# Revit family: ICV-201G
name_source: partatom
category: Pipe Accessories
revit_build: Autodesk Revit 2017 (Build: 20160225_1515(x64)
units: mm (PartAtom-declared; Revit-internal decimal feet)

## family parameters
Always vertical = Yes
Cut with Voids When Loaded = Yes
OmniClass Number = 23.27.31.27
OmniClass Title = Globe Valves
Part Type = Valve - Normal
Round Connector Dimension = Use Diameter
Shared = No
Work Plane-Based = No

## types (6) — shared parameters
Assembly Code = G2050700
Body Material = Hunter® ABS Plastic
Current = 0 A
Filter Sentry = Factory Installed Filter Sentry ™
Flow = 150.0 L/min
Flow Max = 750.0 L/min
Flow Min = 150.0 L/min
Flow_Value = 150.0 L/min
Frequency = 60 Hz
Height = 180 mm  [stored 0.590551 ft]
Inlet Diameter = 2" (50mm)
Inner Diameter = 50 mm  [stored 0.164042 ft]
Keynote = 328423.01
Length = 170 mm  [stored 0.557743 ft]
Loss Method = K Coefficient
Manufacturer = Hunter® Industries
Outer Diameter = 63 mm  [stored 0.206693 ft]
Pipe Diameter = 63 mm  [stored 0.206693 ft]
Power = 8 VA
Power Factor = 1
Pressure Loss = 5.0 kPa
Show Valve Box = Yes
Solenoid Type = inrush
Solenoid VAC = 24 V
Tag Name = ICV-201G
Type Comments = ICV Valve
Type Image = <None>
URL = https://www.hunterindustries.com
Valid Flow = 150.0 L/min
Valve Box = Valve Box
Width = 140 mm  [stored 0.459318 ft]
zero-valued in all types: K Coefficient

## per-type parameters (varying)
| type | Accu Sync® | Accu-Sync URL | AccuSync | Description | K Coefficient Table | Max_Pressure | Min_Pressure | Model |
| ICV-201G-FS |  | ------ | without AccuSync | High Pressure Commercial System Valve ICV-201G with Filter Sentry ™ |  | 1500.0 kPa | 150.0 kPa | ICV-201G-FS |
| ICV-201G-FS-AS-ADJ Black-Adjustable Pressure | Accu Sync® AS-ADJ Black Adjustable Pressure Regulator | https://www.hunterindustries.com | AccuSync Adjustable | High Pressure Commercial System Valve ICV-201G with Filter Sentry ™ and Accu Sync® AS-ADJ Black Adjustable Pressure Regulator | Globe Valve Threaded | 700.0 kPa | 140.0 kPa | ICV-201G-FS-AS-ADJ |
| ICV-201G-FS-AS-30 Red-2.1bar | Accu Sync® Fixed AS-30 Red Fixed Pressure Regulator at 2.1 bar | https://www.hunterindustries.com | AccuSync fixed | High Pressure Commercial System Valve ICV-201G with Filter Sentry ™ and Accu Sync® AS-30 Red Fixed Pressure Regulator |  | 210.0 kPa | 210.0 kPa | ICV-201G-FS-AS-30 |
| ICV-201G-FS-AS-40 Grey-2.8bar | Accu Sync® AS-40 Grey Fixed Pressure Regulator at 2.8 bar | https://www.hunterindustries.com | AccuSync fixed | High Pressure Commercial System Valve ICV-201G with Filter Sentry ™ and Accu Sync® AS-40 Grey Fixed Pressure Regulator |  | 280.0 kPa | 280.0 kPa | ICV-201G-FS-AS-40 |
| ICV-201G-FS-AS-50 Blue-3.5bar | Accu Sync® AS-50 Blue  Fixed Pressure Regulator at 3.5 bar | https://www.hunterindustries.com | AccuSync fixed | High Pressure Commercial System Valve ICV-201G with Filter Sentry ™ and Accu Sync® AS-50 Blue Fixed Pressure Regulator |  | 350.0 kPa | 350.0 kPa | ICV-201G-FS-AS-50 |
| ICV-201G-FS-AS-70 Green-4.8bar | Accu Sync® AS-70 Green Fixed Pressure Regulator at 4.8 bar | https://www.hunterindustries.com | AccuSync fixed | High Pressure Commercial System Valve ICV-201G with Filter Sentry ™ and Accu Sync® AS-70 Green Fixed Pressure Regulator |  | 480.0 kPa | 480.0 kPa | ICV-201G-FS-AS-70 |

note: [stored X ft] marks values corroborated as IEEE doubles in the binary element streams (Revit-internal decimal feet)

## geometry (parser evidence)
native form markers: Sweep x19
no freeform markers — native parametric forms only
